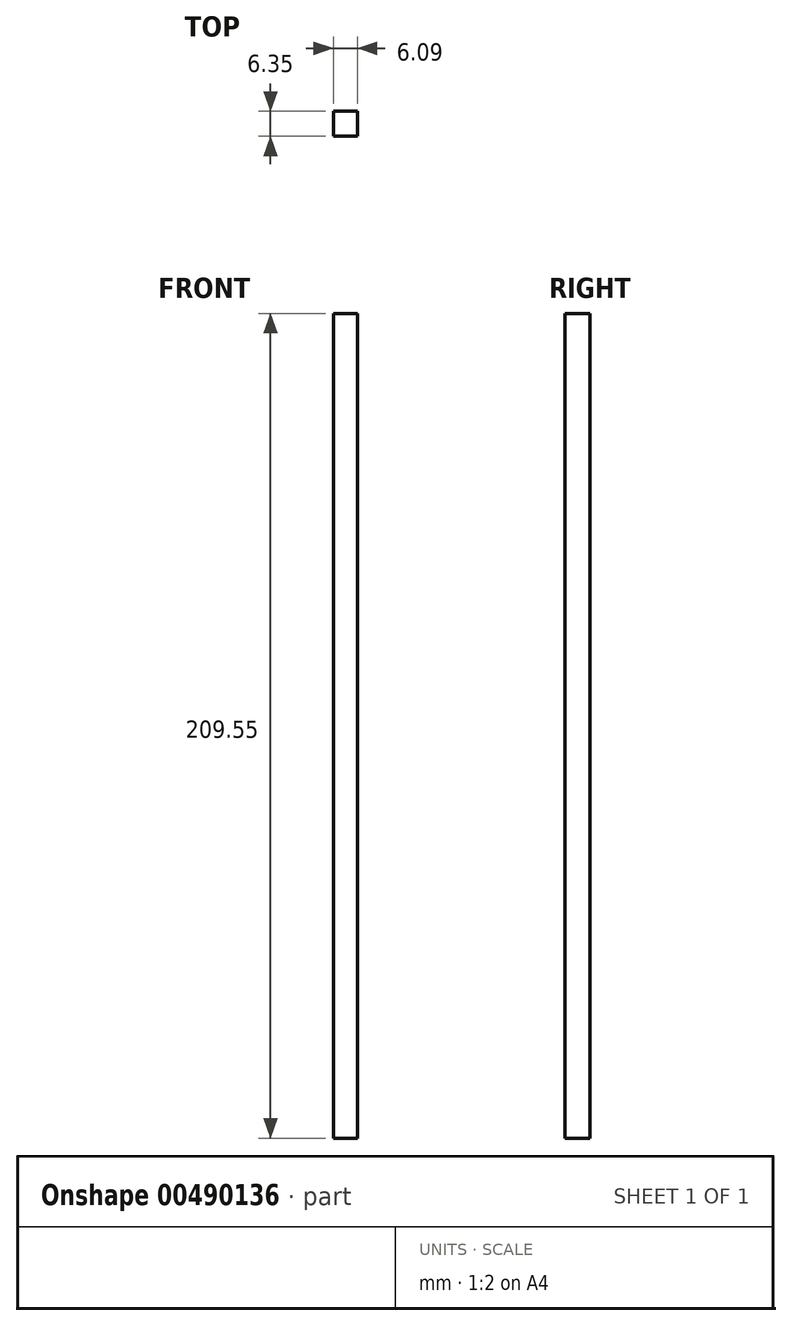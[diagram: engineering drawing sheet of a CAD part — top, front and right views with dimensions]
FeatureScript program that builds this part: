
annotation { "Feature Type Name" : "Feature", "Feature Type Description" : "" }
export const myFeature = defineFeature(function(context is Context, id is Id, definition is map)
    precondition{}
    {
        {
            var Q0;
            Q0=qCreatedBy(makeId("Front.planeOp"),FACE);
            var sketch = newSketch(context, id + "F0", { "sketchPlane" : qUnion([Q0])});
            skLineSegment(sketch, "E0.bottom", {"start": v(-56.35, 190.52) * mm, "end": v(-50.26, 190.52) * mm});
            skLineSegment(sketch, "E0.top", {"start": v(-56.35, -19.03) * mm, "end": v(-50.26, -19.03) * mm});
            skLineSegment(sketch, "E0.left", {"start": v(-56.35, 190.52) * mm, "end": v(-56.35, -19.03) * mm});
            skLineSegment(sketch, "E0.right", {"start": v(-50.26, 190.52) * mm, "end": v(-50.26, -19.03) * mm});
            skSolve(sketch);
        }
        {
            var Q0;
            Q0=makeQuery(id+"F0.imprint","IMPRINT",FACE,{"disambiguationData":[TD([[makeQuery(id+"F0.imprint","IMPRINT",EDGE,{"derivedFrom":sQuery(id+"F0.wireOp",EDGE,"E0.bottom")}),-1.0]])]});
            extrude(context, id + "F1", {"entities" : qUnion([Q0]), "depth" : 6.35 * mm});
        }
    });
